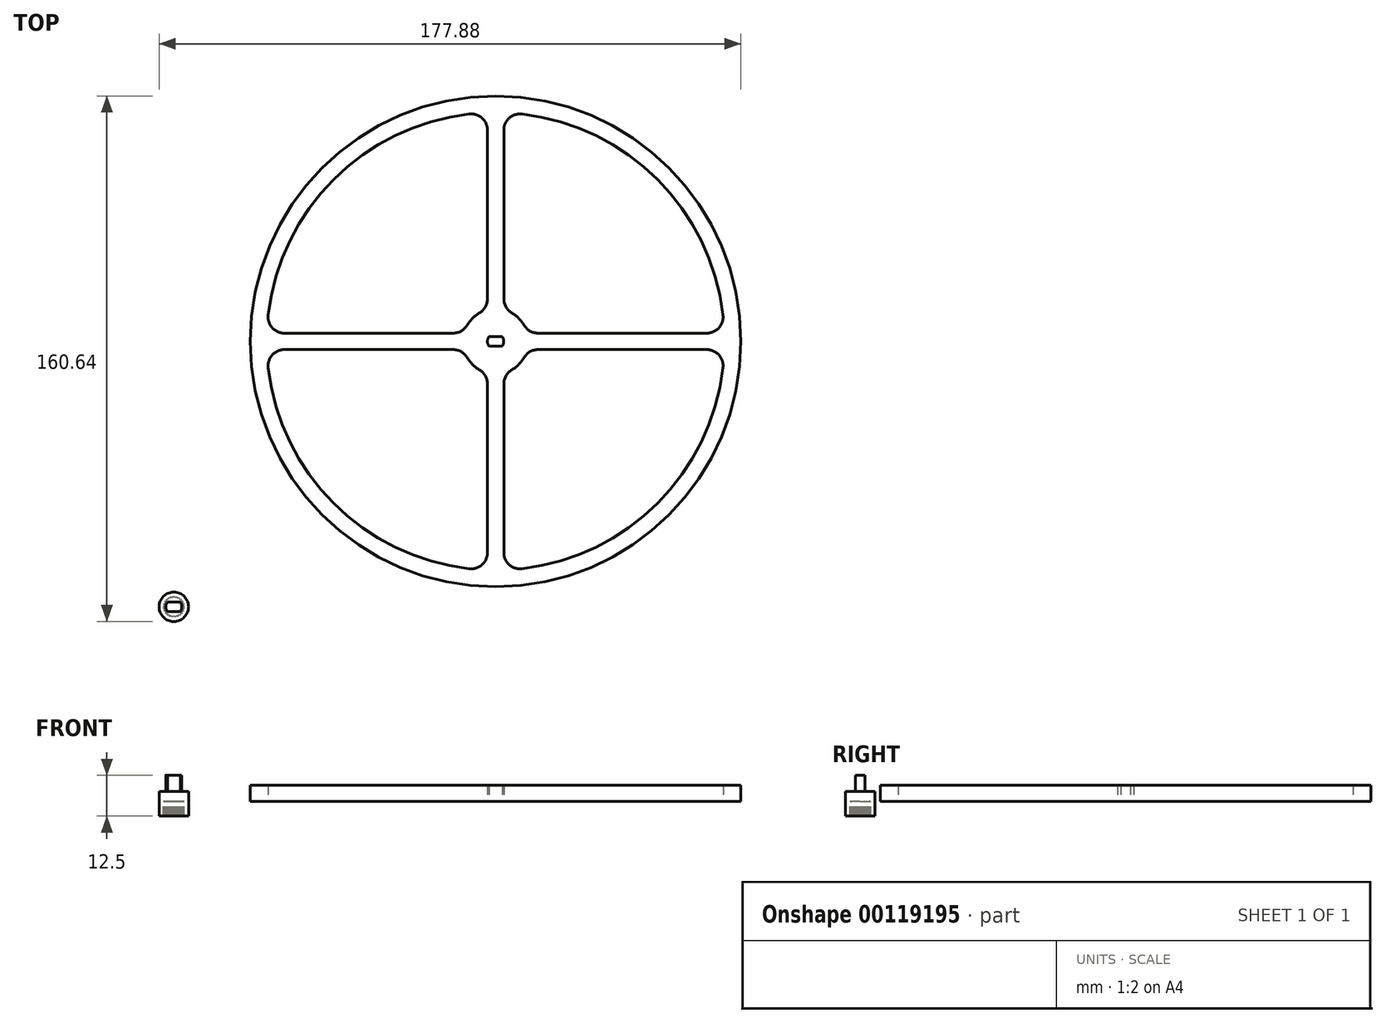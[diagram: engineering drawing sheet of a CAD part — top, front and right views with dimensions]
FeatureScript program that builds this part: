
annotation { "Feature Type Name" : "Feature", "Feature Type Description" : "" }
export const myFeature = defineFeature(function(context is Context, id is Id, definition is map)
    precondition{}
    {
        {
            var Q0;
            Q0=qCreatedBy(makeId("Top.planeOp"),FACE);
            var sketch = newSketch(context, id + "F0", { "sketchPlane" : qUnion([Q0])});
            skCircle(sketch, "E0", {"center": v(0, 0) * mm, "radius": 75 * mm});
            skArc(sketch, "E1", {"start": v(8.66, 5) * mm, "mid": v(7.07, 7.07) * mm, "end": v(5, 8.66) * mm});
            skArc(sketch, "E2", {"start": v(69.53, 8.08) * mm, "mid": v(49.5, 49.5) * mm, "end": v(8.08, 69.53) * mm});
            skLineSegment(sketch, "E3", {"start": v(0, 10) * mm, "end": v(0, 70) * mm, "construction": true});
            skLineSegment(sketch, "E4", {"start": v(10, 0) * mm, "end": v(70, 0) * mm, "construction": true});
            skLineSegment(sketch, "E5", {"start": v(0, -10) * mm, "end": v(0, -70) * mm, "construction": true});
            skLineSegment(sketch, "E6", {"start": v(-10, 0) * mm, "end": v(-70, 0) * mm, "construction": true});
            skLineSegment(sketch, "E7.bottom", {"start": v(70, 0) * mm, "end": v(10, 0) * mm});
            skLineSegment(sketch, "E7.top", {"start": v(70, 0) * mm, "end": v(10, 0) * mm});
            skLineSegment(sketch, "E7.left", {"start": v(70, 0) * mm, "end": v(70, 0) * mm});
            skLineSegment(sketch, "E7.right", {"start": v(10, 0) * mm, "end": v(10, 0) * mm});
            skPoint(sketch, "E7.middle", {"position": v(40, 0) * mm});
            skLineSegment(sketch, "E8.bottom", {"start": v(13, 2.5) * mm, "end": v(64.57, 2.5) * mm});
            skLineSegment(sketch, "E8.top", {"start": v(13, -2.5) * mm, "end": v(64.57, -2.5) * mm});
            skLineSegment(sketch, "E9.left", {"start": v(2.5, 13) * mm, "end": v(2.5, 64.57) * mm});
            skLineSegment(sketch, "E9.right", {"start": v(-2.5, 13) * mm, "end": v(-2.5, 64.57) * mm});
            skPoint(sketch, "E9.middle", {"position": v(0, 40) * mm});
            skLineSegment(sketch, "E10.bottom", {"start": v(-13, 2.5) * mm, "end": v(-64.57, 2.5) * mm});
            skLineSegment(sketch, "E10.top", {"start": v(-13, -2.5) * mm, "end": v(-64.57, -2.5) * mm});
            skPoint(sketch, "E10.middle", {"position": v(-40, 0) * mm});
            skLineSegment(sketch, "E11.left", {"start": v(-2.5, -13) * mm, "end": v(-2.5, -64.57) * mm});
            skLineSegment(sketch, "E11.right", {"start": v(2.5, -13) * mm, "end": v(2.5, -64.57) * mm});
            skPoint(sketch, "E11.middle", {"position": v(0, -40) * mm});
            skArc(sketch, "E12.trimOffspring", {"start": v(-5, 8.66) * mm, "mid": v(-7.07, 7.07) * mm, "end": v(-8.66, 5) * mm});
            skArc(sketch, "E13.trimOffspring", {"start": v(-8.08, 69.53) * mm, "mid": v(-49.5, 49.5) * mm, "end": v(-69.53, 8.08) * mm});
            skArc(sketch, "E14.trimOffspring", {"start": v(-69.53, -8.08) * mm, "mid": v(-49.5, -49.5) * mm, "end": v(-8.08, -69.53) * mm});
            skArc(sketch, "E15.trimOffspring", {"start": v(-8.66, -5) * mm, "mid": v(-7.07, -7.07) * mm, "end": v(-5, -8.66) * mm});
            skArc(sketch, "E16.trimOffspring", {"start": v(5, -8.66) * mm, "mid": v(7.07, -7.07) * mm, "end": v(8.66, -5) * mm});
            skArc(sketch, "E17.trimOffspring", {"start": v(8.08, -69.53) * mm, "mid": v(49.5, -49.5) * mm, "end": v(69.53, -8.08) * mm});
            skPoint(sketch, "E18.visualSharp", {"position": v(2.5, 69.96) * mm});
            skArc(sketch, "E18.filletArc", {"start": v(8.08, 69.53) * mm, "mid": v(4.17, 68.3) * mm, "end": v(2.5, 64.57) * mm});
            skPoint(sketch, "E19.visualSharp", {"position": v(-2.5, 69.96) * mm});
            skArc(sketch, "E19.filletArc", {"start": v(-2.5, 64.57) * mm, "mid": v(-4.17, 68.3) * mm, "end": v(-8.08, 69.53) * mm});
            skPoint(sketch, "E20.visualSharp", {"position": v(69.96, 2.5) * mm});
            skArc(sketch, "E20.filletArc", {"start": v(64.57, 2.5) * mm, "mid": v(68.3, 4.17) * mm, "end": v(69.53, 8.08) * mm});
            skPoint(sketch, "E21.visualSharp", {"position": v(69.96, -2.5) * mm});
            skArc(sketch, "E21.filletArc", {"start": v(69.53, -8.08) * mm, "mid": v(68.3, -4.17) * mm, "end": v(64.57, -2.5) * mm});
            skPoint(sketch, "E22.visualSharp", {"position": v(2.5, -69.96) * mm});
            skArc(sketch, "E22.filletArc", {"start": v(2.5, -64.57) * mm, "mid": v(4.17, -68.3) * mm, "end": v(8.08, -69.53) * mm});
            skPoint(sketch, "E23.visualSharp", {"position": v(-2.5, -69.96) * mm});
            skArc(sketch, "E23.filletArc", {"start": v(-8.08, -69.53) * mm, "mid": v(-4.17, -68.3) * mm, "end": v(-2.5, -64.57) * mm});
            skPoint(sketch, "E24.visualSharp", {"position": v(-69.96, 2.5) * mm});
            skArc(sketch, "E24.filletArc", {"start": v(-69.53, 8.08) * mm, "mid": v(-68.3, 4.17) * mm, "end": v(-64.57, 2.5) * mm});
            skPoint(sketch, "E25.visualSharp", {"position": v(-69.96, -2.5) * mm});
            skArc(sketch, "E25.filletArc", {"start": v(-64.57, -2.5) * mm, "mid": v(-68.3, -4.17) * mm, "end": v(-69.53, -8.08) * mm});
            skPoint(sketch, "E26.visualSharp", {"position": v(-9.68, 2.5) * mm});
            skArc(sketch, "E26.filletArc", {"start": v(-13, 2.5) * mm, "mid": v(-10.5, 3.17) * mm, "end": v(-8.66, 5) * mm});
            skPoint(sketch, "E27.visualSharp", {"position": v(-2.5, 9.68) * mm});
            skArc(sketch, "E27.filletArc", {"start": v(-5, 8.66) * mm, "mid": v(-3.17, 10.5) * mm, "end": v(-2.5, 13) * mm});
            skPoint(sketch, "E28.visualSharp", {"position": v(2.5, 9.68) * mm});
            skArc(sketch, "E28.filletArc", {"start": v(2.5, 13) * mm, "mid": v(3.17, 10.5) * mm, "end": v(5, 8.66) * mm});
            skPoint(sketch, "E29.visualSharp", {"position": v(9.68, 2.5) * mm});
            skArc(sketch, "E29.filletArc", {"start": v(8.66, 5) * mm, "mid": v(10.5, 3.17) * mm, "end": v(13, 2.5) * mm});
            skPoint(sketch, "E30.visualSharp", {"position": v(9.68, -2.5) * mm});
            skArc(sketch, "E30.filletArc", {"start": v(13, -2.5) * mm, "mid": v(10.5, -3.17) * mm, "end": v(8.66, -5) * mm});
            skPoint(sketch, "E31.visualSharp", {"position": v(2.5, -9.68) * mm});
            skArc(sketch, "E31.filletArc", {"start": v(5, -8.66) * mm, "mid": v(3.17, -10.5) * mm, "end": v(2.5, -13) * mm});
            skPoint(sketch, "E32.visualSharp", {"position": v(-2.5, -9.68) * mm});
            skArc(sketch, "E32.filletArc", {"start": v(-2.5, -13) * mm, "mid": v(-3.17, -10.5) * mm, "end": v(-5, -8.66) * mm});
            skPoint(sketch, "E33.visualSharp", {"position": v(-9.68, -2.5) * mm});
            skArc(sketch, "E33.filletArc", {"start": v(-8.66, -5) * mm, "mid": v(-10.5, -3.17) * mm, "end": v(-13, -2.5) * mm});
            skArc(sketch, "E34", {"start": v(-2, 1.5) * mm, "mid": v(-2.5, 0) * mm, "end": v(-2, -1.5) * mm});
            skLineSegment(sketch, "E35.bottom", {"start": v(2, -1.5) * mm, "end": v(-2, -1.5) * mm});
            skLineSegment(sketch, "E35.top", {"start": v(2, 1.5) * mm, "end": v(-2, 1.5) * mm});
            skArc(sketch, "E36.trimOffspring", {"start": v(2, -1.5) * mm, "mid": v(2.5, 0) * mm, "end": v(2, 1.5) * mm});
            skSolve(sketch);
        }
        {
            var Q0;
            Q0=makeQuery(id+"F0.imprint","IMPRINT",FACE,{"disambiguationData":[TD([[makeQuery(id+"F0.imprint","IMPRINT",EDGE,{"derivedFrom":sQuery(id+"F0.wireOp",EDGE,"E0")}),1.0]])]});
            extrude(context, id + "F1", {"entities" : qUnion([Q0]), "depth" : 5 * mm});
        }
        {
            var Q0;
            Q0=qCreatedBy(makeId("Top.planeOp"),FACE);
            var sketch = newSketch(context, id + "F2", { "sketchPlane" : qUnion([Q0])});
            skCircle(sketch, "E37", {"center": v(-98.38, -81.14) * mm, "radius": 4.5 * mm});
            skArc(sketch, "E38", {"start": v(-100.12, -78.82) * mm, "mid": v(-101.03, -79.95) * mm, "end": v(-101.27, -81.37) * mm});
            skLineSegment(sketch, "E39", {"start": v(-98.7, -78.26) * mm, "end": v(-98.38, -77.94) * mm});
            skLineSegment(sketch, "E40", {"start": v(-98.38, -77.94) * mm, "end": v(-98.06, -78.26) * mm});
            skLineSegment(sketch, "E41.1.0", {"start": v(-99.41, -78.43) * mm, "end": v(-99.18, -78.04) * mm});
            skLineSegment(sketch, "E41.1.1", {"start": v(-99.18, -78.04) * mm, "end": v(-98.8, -78.27) * mm});
            skLineSegment(sketch, "E41.2.0", {"start": v(-100.05, -78.77) * mm, "end": v(-99.93, -78.34) * mm});
            skLineSegment(sketch, "E41.2.1", {"start": v(-99.93, -78.34) * mm, "end": v(-99.5, -78.46) * mm});
            skLineSegment(sketch, "E41.3.0", {"start": v(-100.59, -79.26) * mm, "end": v(-100.58, -78.8) * mm});
            skLineSegment(sketch, "E41.3.1", {"start": v(-100.58, -78.8) * mm, "end": v(-100.12, -78.82) * mm});
            skLineSegment(sketch, "E41.4.0", {"start": v(-100.99, -79.87) * mm, "end": v(-101.09, -79.43) * mm});
            skLineSegment(sketch, "E41.4.1", {"start": v(-101.09, -79.43) * mm, "end": v(-100.65, -79.33) * mm});
            skLineSegment(sketch, "E41.5.0", {"start": v(-101.22, -80.56) * mm, "end": v(-101.43, -80.15) * mm});
            skLineSegment(sketch, "E41.5.1", {"start": v(-101.43, -80.15) * mm, "end": v(-101.03, -79.95) * mm});
            skLineSegment(sketch, "E41.6.0", {"start": v(-101.28, -81.28) * mm, "end": v(-101.58, -80.94) * mm});
            skLineSegment(sketch, "E41.6.1", {"start": v(-101.58, -80.94) * mm, "end": v(-101.24, -80.64) * mm});
            skLineSegment(sketch, "E41.7.0", {"start": v(-101.15, -82) * mm, "end": v(-101.53, -81.74) * mm});
            skLineSegment(sketch, "E41.7.1", {"start": v(-101.53, -81.74) * mm, "end": v(-101.27, -81.37) * mm});
            skLineSegment(sketch, "E41.8.0", {"start": v(-100.86, -82.66) * mm, "end": v(-101.28, -82.5) * mm});
            skLineSegment(sketch, "E41.8.1", {"start": v(-101.28, -82.5) * mm, "end": v(-101.13, -82.08) * mm});
            skLineSegment(sketch, "E41.9.0", {"start": v(-100.4, -83.23) * mm, "end": v(-100.85, -83.18) * mm});
            skLineSegment(sketch, "E41.9.1", {"start": v(-100.85, -83.18) * mm, "end": v(-100.8, -82.73) * mm});
            skLineSegment(sketch, "E41.10.0", {"start": v(-99.82, -83.66) * mm, "end": v(-100.27, -83.73) * mm});
            skLineSegment(sketch, "E41.10.1", {"start": v(-100.27, -83.73) * mm, "end": v(-100.34, -83.29) * mm});
            skLineSegment(sketch, "E41.11.0", {"start": v(-99.15, -83.94) * mm, "end": v(-99.56, -84.12) * mm});
            skLineSegment(sketch, "E41.11.1", {"start": v(-99.56, -84.12) * mm, "end": v(-99.74, -83.7) * mm});
            skLineSegment(sketch, "E41.12.0", {"start": v(-98.43, -84.04) * mm, "end": v(-98.78, -84.32) * mm});
            skLineSegment(sketch, "E41.12.1", {"start": v(-98.78, -84.32) * mm, "end": v(-99.06, -83.96) * mm});
            skLineSegment(sketch, "E41.13.0", {"start": v(-97.7, -83.96) * mm, "end": v(-97.98, -84.32) * mm});
            skLineSegment(sketch, "E41.13.1", {"start": v(-97.98, -84.32) * mm, "end": v(-98.34, -84.04) * mm});
            skLineSegment(sketch, "E41.14.0", {"start": v(-97.03, -83.7) * mm, "end": v(-97.2, -84.12) * mm});
            skLineSegment(sketch, "E41.14.1", {"start": v(-97.2, -84.12) * mm, "end": v(-97.62, -83.94) * mm});
            skLineSegment(sketch, "E41.15.0", {"start": v(-96.43, -83.29) * mm, "end": v(-96.5, -83.73) * mm});
            skLineSegment(sketch, "E41.15.1", {"start": v(-96.5, -83.73) * mm, "end": v(-96.95, -83.66) * mm});
            skLineSegment(sketch, "E41.16.0", {"start": v(-95.96, -82.73) * mm, "end": v(-95.92, -83.18) * mm});
            skLineSegment(sketch, "E41.16.1", {"start": v(-95.92, -83.18) * mm, "end": v(-96.37, -83.23) * mm});
            skLineSegment(sketch, "E41.17.0", {"start": v(-95.64, -82.08) * mm, "end": v(-95.49, -82.5) * mm});
            skLineSegment(sketch, "E41.17.1", {"start": v(-95.49, -82.5) * mm, "end": v(-95.91, -82.66) * mm});
            skLineSegment(sketch, "E41.18.0", {"start": v(-95.5, -81.37) * mm, "end": v(-95.24, -81.74) * mm});
            skLineSegment(sketch, "E41.18.1", {"start": v(-95.24, -81.74) * mm, "end": v(-95.61, -82) * mm});
            skLineSegment(sketch, "E41.19.0", {"start": v(-95.53, -80.64) * mm, "end": v(-95.19, -80.94) * mm});
            skLineSegment(sketch, "E41.19.1", {"start": v(-95.19, -80.94) * mm, "end": v(-95.49, -81.28) * mm});
            skLineSegment(sketch, "E41.20.0", {"start": v(-95.74, -79.95) * mm, "end": v(-95.34, -80.15) * mm});
            skLineSegment(sketch, "E41.20.1", {"start": v(-95.34, -80.15) * mm, "end": v(-95.54, -80.56) * mm});
            skLineSegment(sketch, "E41.21.0", {"start": v(-96.12, -79.33) * mm, "end": v(-95.68, -79.43) * mm});
            skLineSegment(sketch, "E41.21.1", {"start": v(-95.68, -79.43) * mm, "end": v(-95.78, -79.87) * mm});
            skLineSegment(sketch, "E41.22.0", {"start": v(-96.64, -78.82) * mm, "end": v(-96.2, -78.8) * mm});
            skLineSegment(sketch, "E41.22.1", {"start": v(-96.2, -78.8) * mm, "end": v(-96.18, -79.26) * mm});
            skLineSegment(sketch, "E41.23.0", {"start": v(-97.28, -78.46) * mm, "end": v(-96.84, -78.34) * mm});
            skLineSegment(sketch, "E41.23.1", {"start": v(-96.84, -78.34) * mm, "end": v(-96.71, -78.77) * mm});
            skLineSegment(sketch, "E41.24.0", {"start": v(-97.98, -78.27) * mm, "end": v(-97.59, -78.04) * mm});
            skLineSegment(sketch, "E41.24.1", {"start": v(-97.59, -78.04) * mm, "end": v(-97.36, -78.43) * mm});
            skArc(sketch, "E42.trimOffspring", {"start": v(-99.5, -78.46) * mm, "mid": v(-97.32, -83.84) * mm, "end": v(-99.41, -78.43) * mm});
            skArc(sketch, "E43.trimOffspring", {"start": v(-98.06, -78.26) * mm, "mid": v(-98.75, -84.02) * mm, "end": v(-97.98, -78.27) * mm});
            skArc(sketch, "E44.trimOffspring", {"start": v(-96.71, -78.77) * mm, "mid": v(-100.09, -83.49) * mm, "end": v(-96.64, -78.82) * mm});
            skArc(sketch, "E45.trimOffspring", {"start": v(-100.65, -79.33) * mm, "mid": v(-96.15, -83) * mm, "end": v(-100.59, -79.26) * mm});
            skArc(sketch, "E46.trimOffspring", {"start": v(-101.03, -79.95) * mm, "mid": v(-101.15, -80.29) * mm, "end": v(-101.24, -80.64) * mm});
            skArc(sketch, "E47.trimOffspring", {"start": v(-101.24, -80.64) * mm, "mid": v(-101.28, -81) * mm, "end": v(-101.27, -81.37) * mm});
            skArc(sketch, "E48.trimOffspring", {"start": v(-101.15, -82) * mm, "mid": v(-95.53, -80.64) * mm, "end": v(-101.28, -81.28) * mm});
            skArc(sketch, "E49.trimOffspring", {"start": v(-101.13, -82.08) * mm, "mid": v(-95.63, -80.25) * mm, "end": v(-101.15, -82) * mm});
            skArc(sketch, "E50.trimOffspring", {"start": v(-100.8, -82.73) * mm, "mid": v(-95.94, -79.59) * mm, "end": v(-100.86, -82.66) * mm});
            skArc(sketch, "E51.trimOffspring", {"start": v(-100.34, -83.29) * mm, "mid": v(-96.4, -79.03) * mm, "end": v(-100.4, -83.23) * mm});
            skArc(sketch, "E52.trimOffspring", {"start": v(-99.74, -83.7) * mm, "mid": v(-96.99, -78.6) * mm, "end": v(-99.82, -83.66) * mm});
            skArc(sketch, "E53.trimOffspring", {"start": v(-99.06, -83.96) * mm, "mid": v(-97.66, -78.33) * mm, "end": v(-99.15, -83.94) * mm});
            skArc(sketch, "E54.trimOffspring", {"start": v(-98.34, -84.04) * mm, "mid": v(-98.38, -78.24) * mm, "end": v(-98.43, -84.04) * mm});
            skArc(sketch, "E55.trimOffspring", {"start": v(-97.62, -83.94) * mm, "mid": v(-96.43, -79) * mm, "end": v(-101.24, -80.64) * mm});
            skArc(sketch, "E56.trimOffspring", {"start": v(-96.95, -83.66) * mm, "mid": v(-97.03, -78.58) * mm, "end": v(-101.27, -81.37) * mm});
            skArc(sketch, "E57.trimOffspring", {"start": v(-96.37, -83.23) * mm, "mid": v(-97.36, -78.43) * mm, "end": v(-101.27, -81.37) * mm});
            skArc(sketch, "E58.trimOffspring", {"start": v(-95.91, -82.66) * mm, "mid": v(-100.83, -79.59) * mm, "end": v(-95.96, -82.73) * mm});
            skArc(sketch, "E59.trimOffspring", {"start": v(-95.61, -82) * mm, "mid": v(-101.14, -80.25) * mm, "end": v(-95.64, -82.08) * mm});
            skArc(sketch, "E60.trimOffspring", {"start": v(-95.49, -81.28) * mm, "mid": v(-101.28, -80.96) * mm, "end": v(-95.5, -81.37) * mm});
            skArc(sketch, "E61.trimOffspring", {"start": v(-95.54, -80.56) * mm, "mid": v(-101.23, -81.68) * mm, "end": v(-95.53, -80.64) * mm});
            skArc(sketch, "E62.trimOffspring", {"start": v(-95.78, -79.87) * mm, "mid": v(-101, -82.38) * mm, "end": v(-95.74, -79.95) * mm});
            skArc(sketch, "E63.trimOffspring", {"start": v(-96.18, -79.26) * mm, "mid": v(-99.5, -78.46) * mm, "end": v(-101.27, -81.37) * mm});
            skArc(sketch, "E64.trimOffspring", {"start": v(-101.15, -82) * mm, "mid": v(-99.15, -83.94) * mm, "end": v(-96.43, -83.29) * mm});
            skArc(sketch, "E65.trimOffspring", {"start": v(-101.15, -82) * mm, "mid": v(-99.5, -83.82) * mm, "end": v(-97.03, -83.7) * mm});
            skArc(sketch, "E66.trimOffspring", {"start": v(-101.15, -82) * mm, "mid": v(-95.49, -81) * mm, "end": v(-101.22, -80.56) * mm});
            skArc(sketch, "E67.trimOffspring", {"start": v(-101.15, -82) * mm, "mid": v(-95.64, -82.08) * mm, "end": v(-100.05, -78.77) * mm});
            skArc(sketch, "E68.trimOffspring", {"start": v(-101.15, -82) * mm, "mid": v(-97.03, -83.7) * mm, "end": v(-96.12, -79.33) * mm});
            skArc(sketch, "E69.trimOffspring", {"start": v(-101.15, -82) * mm, "mid": v(-99.82, -83.66) * mm, "end": v(-97.7, -83.96) * mm});
            skArc(sketch, "E70.trimOffspring", {"start": v(-101.15, -82) * mm, "mid": v(-95.5, -81.37) * mm, "end": v(-100.99, -79.87) * mm});
            skSolve(sketch);
        }
        {
            var Q0;
            Q0=makeQuery(id+"F2.imprint","IMPRINT",FACE,{"disambiguationData":[TD([[makeQuery(id+"F2.imprint","IMPRINT",EDGE,{"derivedFrom":sQuery(id+"F2.wireOp",EDGE,"E37")}),1.0]])]});
            extrude(context, id + "F3", {"entities" : qUnion([Q0]), "oppositeDirection" : true, "depth" : 4.5 * mm});
        }
        {
            var Q0;
            Q0=makeQuery(id+"F2.imprint","IMPRINT",FACE,{"disambiguationData":[TD([[makeQuery(id+"F2.imprint","IMPRINT",EDGE,{"derivedFrom":sQuery(id+"F2.wireOp",EDGE,"E37")}),1.0]])]});
            var Q1;
            {var subQ29=sQuery(id+"F2.wireOp",EDGE,"E38");Q1=makeQuery(id+"F2.imprint","IMPRINT",FACE,{"disambiguationData":[TD([[makeQuery(id+"F2.imprint","IMPRINT",EDGE,{"derivedFrom":subQ29}),1.0]])]});}
            var Q2;
            {var subQ35=sQuery(id+"F2.wireOp",EDGE,"E62.trimOffspring");Q2=makeQuery(id+"F2.imprint","IMPRINT",FACE,{"disambiguationData":[TD([[makeQuery(id+"F2.imprint","IMPRINT",EDGE,{"derivedFrom":subQ35}),1.0]])]});}
            var Q3;
            {var subQ0=sQuery(id+"F2.wireOp",EDGE,"E41.3.0");Q3=makeQuery(id+"F2.imprint","IMPRINT",FACE,{"disambiguationData":[TD([[makeQuery(id+"F2.imprint","IMPRINT",EDGE,{"derivedFrom":subQ0}),-1.0]])]});}
            var Q4;
            {var subQ0=sQuery(id+"F2.wireOp",EDGE,"E41.2.0");Q4=makeQuery(id+"F2.imprint","IMPRINT",FACE,{"disambiguationData":[TD([[makeQuery(id+"F2.imprint","IMPRINT",EDGE,{"derivedFrom":subQ0}),-1.0]])]});}
            var Q5;
            {var subQ0=sQuery(id+"F2.wireOp",EDGE,"E41.1.0");Q5=makeQuery(id+"F2.imprint","IMPRINT",FACE,{"disambiguationData":[TD([[makeQuery(id+"F2.imprint","IMPRINT",EDGE,{"derivedFrom":subQ0}),-1.0]])]});}
            var Q6;
            {var subQ0=sQuery(id+"F2.wireOp",EDGE,"E39");Q6=makeQuery(id+"F2.imprint","IMPRINT",FACE,{"disambiguationData":[TD([[makeQuery(id+"F2.imprint","IMPRINT",EDGE,{"derivedFrom":subQ0}),-1.0]])]});}
            var Q7;
            {var subQ0=sQuery(id+"F2.wireOp",EDGE,"E41.24.0");Q7=makeQuery(id+"F2.imprint","IMPRINT",FACE,{"disambiguationData":[TD([[makeQuery(id+"F2.imprint","IMPRINT",EDGE,{"derivedFrom":subQ0}),-1.0]])]});}
            var Q8;
            {var subQ0=sQuery(id+"F2.wireOp",EDGE,"E41.23.0");Q8=makeQuery(id+"F2.imprint","IMPRINT",FACE,{"disambiguationData":[TD([[makeQuery(id+"F2.imprint","IMPRINT",EDGE,{"derivedFrom":subQ0}),-1.0]])]});}
            var Q9;
            {var subQ0=sQuery(id+"F2.wireOp",EDGE,"E41.22.0");Q9=makeQuery(id+"F2.imprint","IMPRINT",FACE,{"disambiguationData":[TD([[makeQuery(id+"F2.imprint","IMPRINT",EDGE,{"derivedFrom":subQ0}),-1.0]])]});}
            var Q10;
            {var subQ0=sQuery(id+"F2.wireOp",EDGE,"E41.21.0");Q10=makeQuery(id+"F2.imprint","IMPRINT",FACE,{"disambiguationData":[TD([[makeQuery(id+"F2.imprint","IMPRINT",EDGE,{"derivedFrom":subQ0}),-1.0]])]});}
            var Q11;
            {var subQ0=sQuery(id+"F2.wireOp",EDGE,"E41.20.0");Q11=makeQuery(id+"F2.imprint","IMPRINT",FACE,{"disambiguationData":[TD([[makeQuery(id+"F2.imprint","IMPRINT",EDGE,{"derivedFrom":subQ0}),-1.0]])]});}
            var Q12;
            {var subQ0=sQuery(id+"F2.wireOp",EDGE,"E41.19.0");Q12=makeQuery(id+"F2.imprint","IMPRINT",FACE,{"disambiguationData":[TD([[makeQuery(id+"F2.imprint","IMPRINT",EDGE,{"derivedFrom":subQ0}),-1.0]])]});}
            var Q13;
            {var subQ0=sQuery(id+"F2.wireOp",EDGE,"E41.18.0");Q13=makeQuery(id+"F2.imprint","IMPRINT",FACE,{"disambiguationData":[TD([[makeQuery(id+"F2.imprint","IMPRINT",EDGE,{"derivedFrom":subQ0}),-1.0]])]});}
            var Q14;
            {var subQ0=sQuery(id+"F2.wireOp",EDGE,"E41.17.0");Q14=makeQuery(id+"F2.imprint","IMPRINT",FACE,{"disambiguationData":[TD([[makeQuery(id+"F2.imprint","IMPRINT",EDGE,{"derivedFrom":subQ0}),-1.0]])]});}
            var Q15;
            {var subQ0=sQuery(id+"F2.wireOp",EDGE,"E41.16.0");Q15=makeQuery(id+"F2.imprint","IMPRINT",FACE,{"disambiguationData":[TD([[makeQuery(id+"F2.imprint","IMPRINT",EDGE,{"derivedFrom":subQ0}),-1.0]])]});}
            var Q16;
            {var subQ0=sQuery(id+"F2.wireOp",EDGE,"E41.15.0");Q16=makeQuery(id+"F2.imprint","IMPRINT",FACE,{"disambiguationData":[TD([[makeQuery(id+"F2.imprint","IMPRINT",EDGE,{"derivedFrom":subQ0}),-1.0]])]});}
            var Q17;
            {var subQ0=sQuery(id+"F2.wireOp",EDGE,"E41.14.0");Q17=makeQuery(id+"F2.imprint","IMPRINT",FACE,{"disambiguationData":[TD([[makeQuery(id+"F2.imprint","IMPRINT",EDGE,{"derivedFrom":subQ0}),-1.0]])]});}
            var Q18;
            {var subQ0=sQuery(id+"F2.wireOp",EDGE,"E41.4.0");Q18=makeQuery(id+"F2.imprint","IMPRINT",FACE,{"disambiguationData":[TD([[makeQuery(id+"F2.imprint","IMPRINT",EDGE,{"derivedFrom":subQ0}),-1.0]])]});}
            var Q19;
            {var subQ0=sQuery(id+"F2.wireOp",EDGE,"E41.5.0");Q19=makeQuery(id+"F2.imprint","IMPRINT",FACE,{"disambiguationData":[TD([[makeQuery(id+"F2.imprint","IMPRINT",EDGE,{"derivedFrom":subQ0}),-1.0]])]});}
            var Q20;
            {var subQ0=sQuery(id+"F2.wireOp",EDGE,"E41.6.0");Q20=makeQuery(id+"F2.imprint","IMPRINT",FACE,{"disambiguationData":[TD([[makeQuery(id+"F2.imprint","IMPRINT",EDGE,{"derivedFrom":subQ0}),-1.0]])]});}
            var Q21;
            Q21=makeQuery(id+"F2.imprint","IMPRINT",FACE,{"disambiguationData":[TD([[makeQuery(id+"F2.imprint","IMPRINT",EDGE,{"derivedFrom":sQuery(id+"F2.wireOp",EDGE,"E41.7.0")}),-1.0]])]});
            var Q22;
            {var subQ0=sQuery(id+"F2.wireOp",EDGE,"E41.8.0");Q22=makeQuery(id+"F2.imprint","IMPRINT",FACE,{"disambiguationData":[TD([[makeQuery(id+"F2.imprint","IMPRINT",EDGE,{"derivedFrom":subQ0}),-1.0]])]});}
            var Q23;
            {var subQ0=sQuery(id+"F2.wireOp",EDGE,"E41.9.0");Q23=makeQuery(id+"F2.imprint","IMPRINT",FACE,{"disambiguationData":[TD([[makeQuery(id+"F2.imprint","IMPRINT",EDGE,{"derivedFrom":subQ0}),-1.0]])]});}
            var Q24;
            {var subQ0=sQuery(id+"F2.wireOp",EDGE,"E41.10.0");Q24=makeQuery(id+"F2.imprint","IMPRINT",FACE,{"disambiguationData":[TD([[makeQuery(id+"F2.imprint","IMPRINT",EDGE,{"derivedFrom":subQ0}),-1.0]])]});}
            var Q25;
            {var subQ0=sQuery(id+"F2.wireOp",EDGE,"E41.11.0");Q25=makeQuery(id+"F2.imprint","IMPRINT",FACE,{"disambiguationData":[TD([[makeQuery(id+"F2.imprint","IMPRINT",EDGE,{"derivedFrom":subQ0}),-1.0]])]});}
            var Q26;
            {var subQ0=sQuery(id+"F2.wireOp",EDGE,"E41.12.0");Q26=makeQuery(id+"F2.imprint","IMPRINT",FACE,{"disambiguationData":[TD([[makeQuery(id+"F2.imprint","IMPRINT",EDGE,{"derivedFrom":subQ0}),-1.0]])]});}
            var Q27;
            {var subQ0=sQuery(id+"F2.wireOp",EDGE,"E41.13.0");Q27=makeQuery(id+"F2.imprint","IMPRINT",FACE,{"disambiguationData":[TD([[makeQuery(id+"F2.imprint","IMPRINT",EDGE,{"derivedFrom":subQ0}),-1.0]])]});}
            extrude(context, id + "F4", {"entities" : qUnion([Q0, Q1, Q2, Q3, Q4, Q5, Q6, Q7, Q8, Q9, Q10, Q11, Q12, Q13, Q14, Q15, Q16, Q17, Q18, Q19, Q20, Q21, Q22, Q23, Q24, Q25, Q26, Q27]), "operationType" : NewBodyOperationType.ADD, "depth" : 3 * mm});
        }
        {
            var Q0;
            Q0=makeQuery(id+"F4.opExtrude","CAP_FACE",FACE,{"disambiguationData":[OSD([sQuery(id+"F2.wireOp",EDGE,"E37")])],"isStart":false});
            var sketch = newSketch(context, id + "F5", { "sketchPlane" : qUnion([Q0])});
            skCircle(sketch, "E71", {"center": v(-98.38, -81.14) * mm, "radius": 2.45 * mm});
            skLineSegment(sketch, "E72.bottom", {"start": v(-96.4, -82.6) * mm, "end": v(-100.36, -82.6) * mm});
            skLineSegment(sketch, "E72.top", {"start": v(-96.4, -79.7) * mm, "end": v(-100.36, -79.7) * mm});
            skLineSegment(sketch, "E72.left", {"start": v(-96.4, -82.6) * mm, "end": v(-96.4, -79.7) * mm});
            skLineSegment(sketch, "E72.right", {"start": v(-100.36, -82.6) * mm, "end": v(-100.36, -79.7) * mm});
            skSolve(sketch);
        }
        {
            var Q0;
            {var subQ0=sQuery(id+"F5.wireOp",EDGE,"E72.left");Q0=makeQuery(id+"F5.imprint","IMPRINT",FACE,{"disambiguationData":[TD([[makeQuery(id+"F5.imprint","IMPRINT",EDGE,{"derivedFrom":subQ0}),-1.0]])]});}
            var Q1;
            Q1=makeQuery(id+"F5.imprint","IMPRINT",FACE,{"disambiguationData":[TD([[makeQuery(id+"F5.imprint","IMPRINT",EDGE,{"derivedFrom":sQuery(id+"F5.wireOp",EDGE,"E72.bottom")}),-1.0]])]});
            var Q2;
            {var subQ0=sQuery(id+"F5.wireOp",EDGE,"E72.right");Q2=makeQuery(id+"F5.imprint","IMPRINT",FACE,{"disambiguationData":[TD([[makeQuery(id+"F5.imprint","IMPRINT",EDGE,{"derivedFrom":subQ0}),1.0]])]});}
            extrude(context, id + "F6", {"entities" : qUnion([Q0, Q1, Q2]), "operationType" : NewBodyOperationType.ADD, "depth" : 5 * mm});
        }
    });
